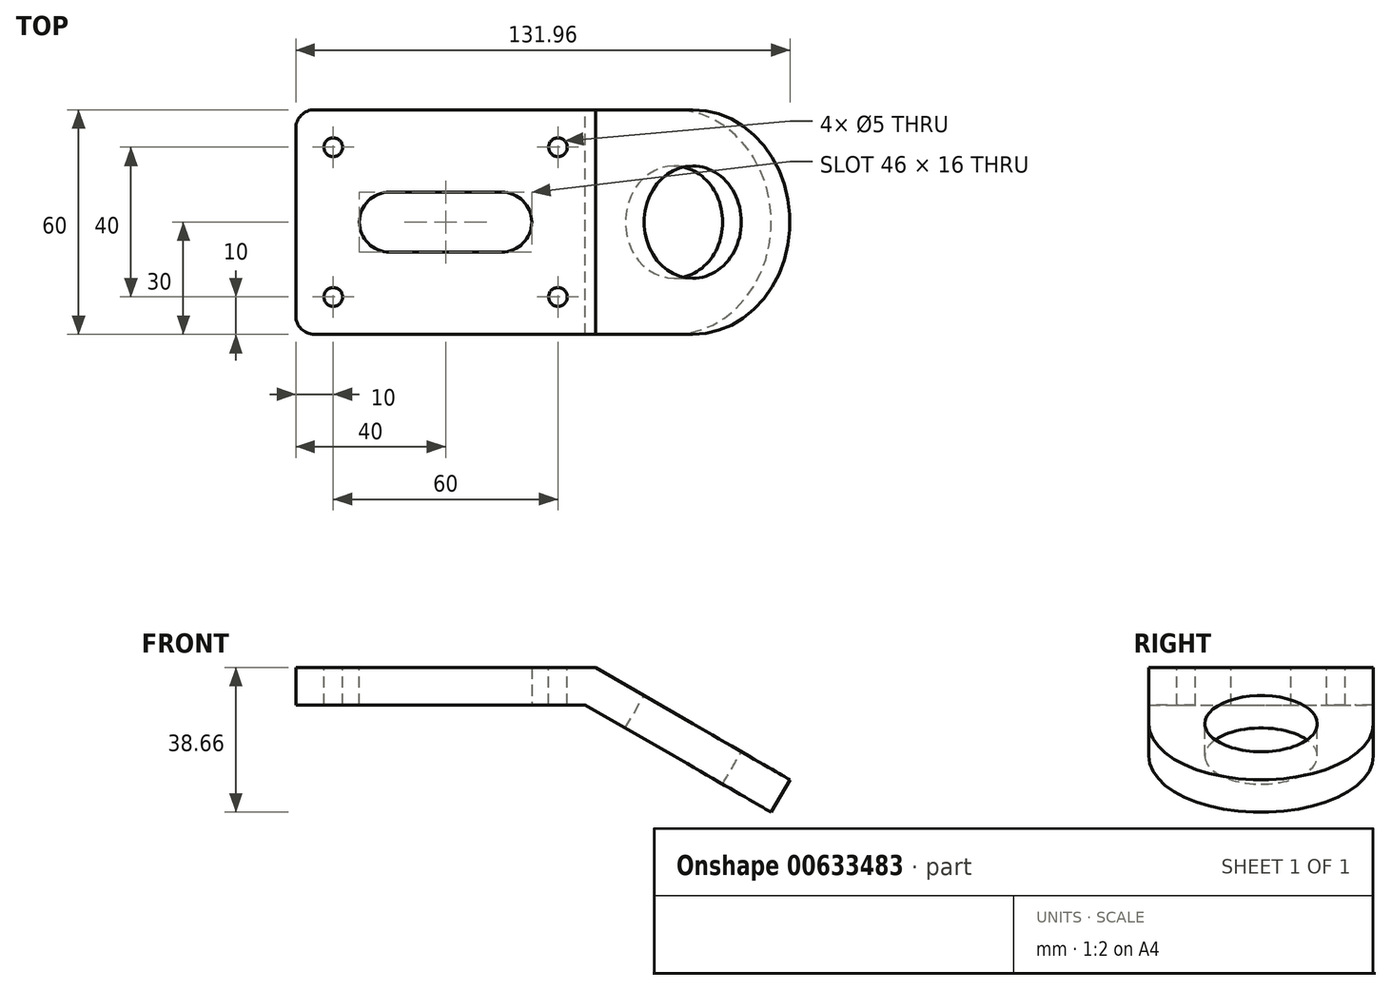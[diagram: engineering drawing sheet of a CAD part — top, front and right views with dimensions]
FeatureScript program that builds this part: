
annotation { "Feature Type Name" : "Feature", "Feature Type Description" : "" }
export const myFeature = defineFeature(function(context is Context, id is Id, definition is map)
    precondition{}
    {
        {
            var Q0;
            Q0=qCreatedBy(makeId("Front.planeOp"),FACE);
            var sketch = newSketch(context, id + "F0", { "sketchPlane" : qUnion([Q0])});
            skLineSegment(sketch, "E0", {"start": v(0, 0) * mm, "end": v(80, 0) * mm});
            skLineSegment(sketch, "E1", {"start": v(80, 0) * mm, "end": v(131.96, -30) * mm});
            skLineSegment(sketch, "E2.0", {"start": v(77.32, -10) * mm, "end": v(126.96, -38.66) * mm});
            skLineSegment(sketch, "E2.1", {"start": v(0, -10) * mm, "end": v(77.32, -10) * mm});
            skLineSegment(sketch, "E3", {"start": v(0, 0) * mm, "end": v(0, -10) * mm});
            skLineSegment(sketch, "E4", {"start": v(131.96, -30) * mm, "end": v(126.96, -38.66) * mm});
            skLineSegment(sketch, "E5", {"start": v(80, 0) * mm, "end": v(77.32, -10) * mm});
            skSolve(sketch);
        }
        {
            var Q0;
            Q0=makeQuery(id+"F0.imprint","IMPRINT",FACE,{"disambiguationData":[TD([[makeQuery(id+"F0.imprint","IMPRINT",EDGE,{"derivedFrom":sQuery(id+"F0.wireOp",EDGE,"E0")}),-1.0]])]});
            var Q1;
            Q1=makeQuery(id+"F0.imprint","IMPRINT",FACE,{"disambiguationData":[TD([[makeQuery(id+"F0.imprint","IMPRINT",EDGE,{"derivedFrom":sQuery(id+"F0.wireOp",EDGE,"E1")}),-1.0]])]});
            extrude(context, id + "F1", {"entities" : qUnion([Q0, Q1]), "depth" : 60 * mm, "offsetDistance" : 25 * mm});
        }
        {
            var Q0;
            Q0=makeQuery(id+"F1.opExtrude","CAP_EDGE",EDGE,{"disambiguationData":[OSD([sQuery(id+"F0.wireOp",EDGE,"E4")])],"isStart":true});
            var Q1;
            Q1=makeQuery(id+"F1.opExtrude","CAP_EDGE",EDGE,{"disambiguationData":[OSD([sQuery(id+"F0.wireOp",EDGE,"E4")])],"isStart":false});
            fillet(context, id + "F2", {"entities" : qUnion([Q0, Q1]), "radius" : 30 * mm, "tangentPropagation" : true, "allowEdgeOverflow" : false});
        }
        {
            var Q0;
            Q0=makeQuery(id+"F1.opExtrude","SWEPT_FACE",FACE,{"disambiguationData":[OSD([sQuery(id+"F0.wireOp",EDGE,"E1")])]});
            var sketch = newSketch(context, id + "F3", { "sketchPlane" : qUnion([Q0])});
            skCircle(sketch, "E6", {"center": v(99.28, -30) * mm, "radius": 15 * mm});
            skSolve(sketch);
        }
        {
            var Q0;
            Q0=makeQuery(id+"F3.imprint","IMPRINT",FACE,{"disambiguationData":[TD([[makeQuery(id+"F3.imprint","IMPRINT",EDGE,{"derivedFrom":sQuery(id+"F3.wireOp",EDGE,"E6")}),1.0]])]});
            extrude(context, id + "F4", {"entities" : qUnion([Q0]), "operationType" : NewBodyOperationType.REMOVE, "oppositeDirection" : true, "depth" : 25 * mm, "offsetDistance" : 25 * mm});
        }
        {
            var Q0;
            Q0=makeQuery(id+"F1.opExtrude","CAP_EDGE",EDGE,{"disambiguationData":[OSD([sQuery(id+"F0.wireOp",EDGE,"E3")])],"isStart":true});
            var Q1;
            Q1=makeQuery(id+"F1.opExtrude","CAP_EDGE",EDGE,{"disambiguationData":[OSD([sQuery(id+"F0.wireOp",EDGE,"E3")])],"isStart":false});
            fillet(context, id + "F5", {"entities" : qUnion([Q0, Q1]), "radius" : 5 * mm, "tangentPropagation" : true, "allowEdgeOverflow" : false});
        }
        {
            var Q0;
            Q0=makeQuery(id+"F1.opExtrude","SWEPT_FACE",FACE,{"disambiguationData":[OSD([sQuery(id+"F0.wireOp",EDGE,"E0")])]});
            var sketch = newSketch(context, id + "F6", { "sketchPlane" : qUnion([Q0])});
            skCircle(sketch, "E7", {"center": v(10, -50) * mm, "radius": 2.5 * mm});
            skCircle(sketch, "E8", {"center": v(70, -50) * mm, "radius": 2.5 * mm});
            skCircle(sketch, "E9", {"center": v(70, -10) * mm, "radius": 2.5 * mm});
            skCircle(sketch, "E10", {"center": v(10, -10) * mm, "radius": 2.5 * mm});
            skLineSegment(sketch, "E11.bottom", {"start": v(63, -38) * mm, "end": v(17, -38) * mm});
            skLineSegment(sketch, "E11.top", {"start": v(63, -22) * mm, "end": v(17, -22) * mm});
            skLineSegment(sketch, "E11.left", {"start": v(63, -38) * mm, "end": v(63, -22) * mm});
            skLineSegment(sketch, "E11.right", {"start": v(17, -38) * mm, "end": v(17, -22) * mm});
            skPoint(sketch, "E11.middle", {"position": v(40, -30) * mm});
            skSolve(sketch);
        }
        {
            var Q0;
            Q0=makeQuery(id+"F6.imprint","IMPRINT",FACE,{"disambiguationData":[TD([[makeQuery(id+"F6.imprint","IMPRINT",EDGE,{"derivedFrom":sQuery(id+"F6.wireOp",EDGE,"E11.bottom")}),-1.0]])]});
            extrude(context, id + "F7", {"entities" : qUnion([Q0]), "operationType" : NewBodyOperationType.REMOVE, "oppositeDirection" : true, "depth" : 25 * mm, "offsetDistance" : 25 * mm});
        }
        {
            var Q0;
            Q0 = qSketchRegion(id + "F6", true);
            extrude(context, id + "F8", {"entities" : qUnion([Q0]), "operationType" : NewBodyOperationType.REMOVE, "oppositeDirection" : true, "depth" : 25 * mm, "offsetDistance" : 25 * mm});
        }
        {
            var Q0;
            Q0=makeQuery(id+"F7.boolean.opBoolean","COPY",EDGE,{"derivedFrom":makeQuery(id+"F7.opExtrude","SWEPT_EDGE",EDGE,{"disambiguationData":[OSD([sQuery(id+"F6.wireOp",EDGE,"E11.top"),sQuery(id+"F6.wireOp",EDGE,"E11.left")])]})});
            var Q1;
            Q1=makeQuery(id+"F7.boolean.opBoolean","COPY",EDGE,{"derivedFrom":makeQuery(id+"F7.opExtrude","SWEPT_EDGE",EDGE,{"disambiguationData":[OSD([sQuery(id+"F6.wireOp",EDGE,"E11.bottom"),sQuery(id+"F6.wireOp",EDGE,"E11.left")])]})});
            var Q2;
            Q2=makeQuery(id+"F7.boolean.opBoolean","COPY",EDGE,{"derivedFrom":makeQuery(id+"F7.opExtrude","SWEPT_EDGE",EDGE,{"disambiguationData":[OSD([sQuery(id+"F6.wireOp",EDGE,"E11.top"),sQuery(id+"F6.wireOp",EDGE,"E11.right")])]})});
            var Q3;
            Q3=makeQuery(id+"F7.boolean.opBoolean","COPY",EDGE,{"derivedFrom":makeQuery(id+"F7.opExtrude","SWEPT_EDGE",EDGE,{"disambiguationData":[OSD([sQuery(id+"F6.wireOp",EDGE,"E11.bottom"),sQuery(id+"F6.wireOp",EDGE,"E11.right")])]})});
            fillet(context, id + "F9", {"entities" : qUnion([Q0, Q1, Q2, Q3]), "radius" : 8 * mm, "tangentPropagation" : true, "allowEdgeOverflow" : false});
        }
    });
